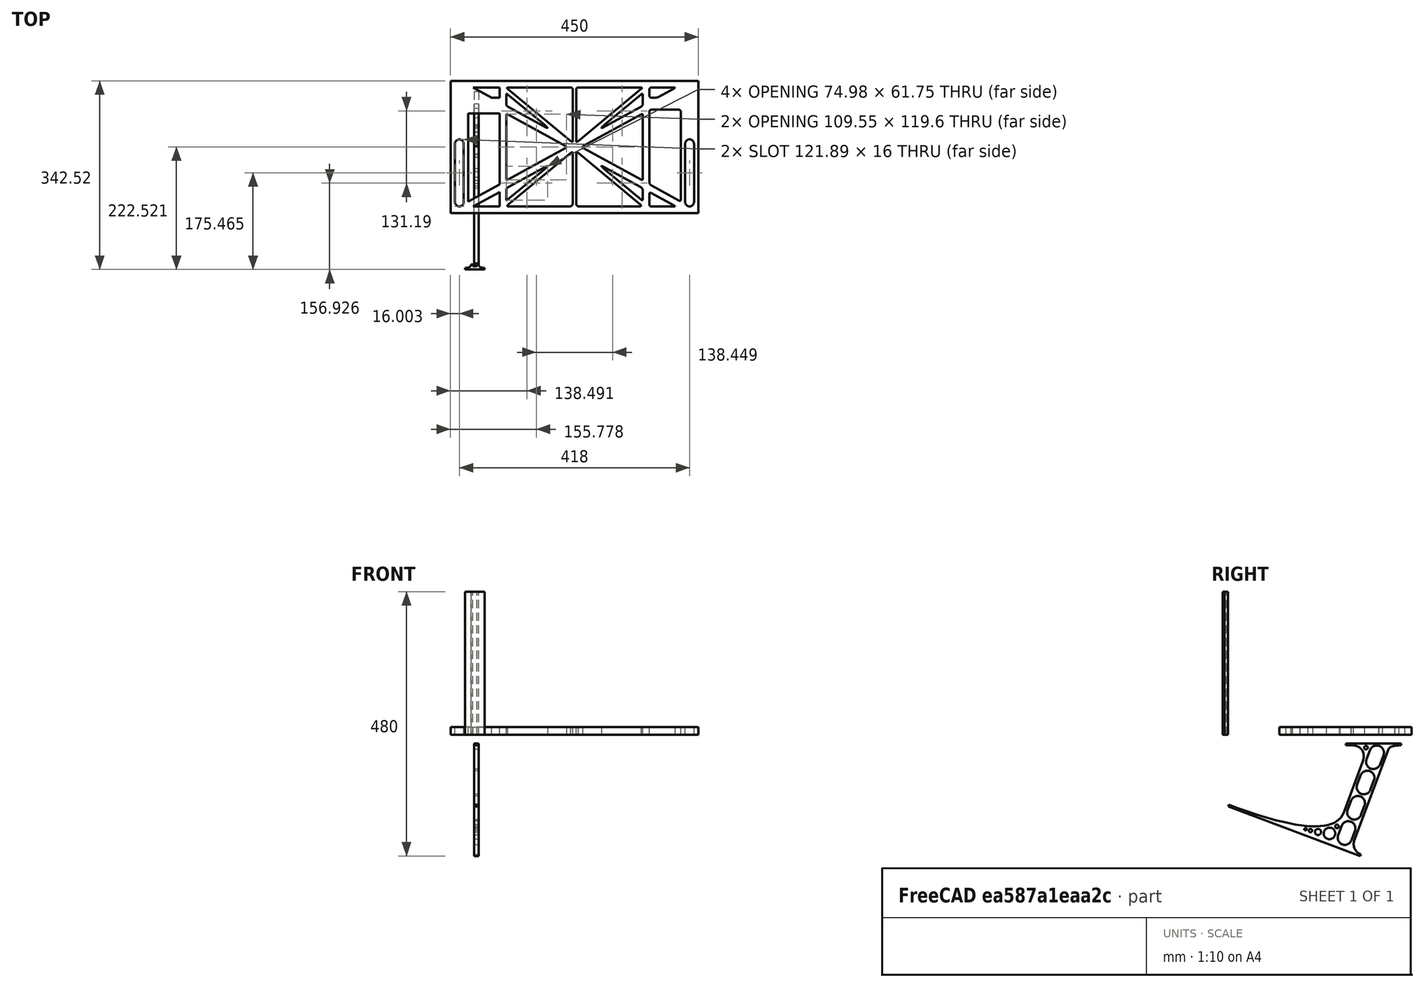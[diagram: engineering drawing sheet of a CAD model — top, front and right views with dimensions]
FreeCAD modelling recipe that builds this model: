
FCSTD DOCUMENT  (FreeCAD 0.19R0.19.2)
Label: laptopStand1155FCStd
License: All rights reserved
LicenseURL: http://en.wikipedia.org/wiki/All_rights_reserved
objects: Sketcher::SketchObject×3, Part::Extrusion×3
note: 6 computed .brp shape members not serialized (recipe doc carries the construction recipe); baked Part::Feature solids carry a one-line shape summary decoded from their .brp

FEATURE [Sketcher::SketchObject] Sketch
  FullyConstrained = true
  sketch-geometry (318):
    g0: LineSegment StartX=-10.9272 StartY=-82.7794 StartZ=0 EndX=46.0728 EndY=-51.4823 EndZ=0
    g1: LineSegment StartX=-10.9272 StartY=77.3346 StartZ=0 EndX=-10.9272 EndY=-82.7794 EndZ=0
    g2: LineSegment StartX=-1.92719 StartY=-91.7794 StartZ=0 EndX=46.0728 EndY=-91.7794 EndZ=0
    g3: LineSegment StartX=46.0728 StartY=-65.424 StartZ=0 EndX=-1.92719 EndY=-91.7794 EndZ=0
    g4: LineSegment StartX=46.0728 StartY=-65.424 StartZ=0 EndX=46.0728 EndY=-91.7794 EndZ=0
    g5: LineSegment StartX=46.0728 StartY=77.3346 StartZ=0 EndX=46.0728 EndY=-51.4823 EndZ=0
    g6: LineSegment StartX=-42.9272 StartY=136.221 StartZ=0 EndX=-42.9272 EndY=-103.779 EndZ=0
    g7: LineSegment StartX=407.073 StartY=136.221 StartZ=0 EndX=407.073 EndY=-103.779 EndZ=0
    g8: ArcOfCircle CenterX=-26.9272 CenterY=22.1087 CenterZ=0 NormalX=0 NormalY=0 NormalZ=1 AngleXU=0 Radius=8 StartAngle=1e-16 EndAngle=3.14159
    g9: ArcOfCircle CenterX=-26.9272 CenterY=-83.7794 CenterZ=0 NormalX=0 NormalY=0 NormalZ=1 AngleXU=0 Radius=8 StartAngle=3.14159 EndAngle=6.28319
    g10: LineSegment StartX=-34.9272 StartY=22.1087 StartZ=0 EndX=-34.9272 EndY=-83.7794 EndZ=0
    g11: LineSegment StartX=-18.9272 StartY=22.1087 StartZ=0 EndX=-18.9272 EndY=-83.7794 EndZ=0
    g12: ArcOfCircle CenterX=391.073 CenterY=22.1087 CenterZ=0 NormalX=0 NormalY=0 NormalZ=1 AngleXU=0 Radius=8 StartAngle=-4.4e-15 EndAngle=3.14159
    g13: LineSegment StartX=399.073 StartY=22.1087 StartZ=0 EndX=399.073 EndY=-83.7794 EndZ=0
    g14: LineSegment StartX=383.073 StartY=22.1087 StartZ=0 EndX=383.073 EndY=-83.7794 EndZ=0
    g15: ArcOfCircle CenterX=391.073 CenterY=-83.7794 CenterZ=0 NormalX=0 NormalY=0 NormalZ=1 AngleXU=0 Radius=8 StartAngle=3.14159 EndAngle=6.28319
    g16: Circle CenterX=175.022 CenterY=27.0628 CenterZ=0 NormalX=0 NormalY=0 NormalZ=1 AngleXU=0 Radius=1
    g17: Circle CenterX=179.022 CenterY=24.8665 CenterZ=0 NormalX=0 NormalY=0 NormalZ=1 AngleXU=0 Radius=1
    g18: Circle CenterX=179.022 CenterY=27.0628 CenterZ=0 NormalX=0 NormalY=0 NormalZ=1 AngleXU=0 Radius=1
    g19: BSplineCurve PolesCount=3 KnotsCount=2 Degree=2 IsPeriodic=0
    g20: GeomPoint X=175.022 Y=27.0628 Z=0
    g21: GeomPoint X=179.022 Y=27.0628 Z=0
    g22: Circle CenterX=189.124 CenterY=27.0628 CenterZ=0 NormalX=0 NormalY=0 NormalZ=1 AngleXU=0 Radius=1
    g23: Circle CenterX=185.124 CenterY=24.8665 CenterZ=0 NormalX=0 NormalY=0 NormalZ=1 AngleXU=0 Radius=1
    g24: Circle CenterX=185.124 CenterY=27.0628 CenterZ=0 NormalX=0 NormalY=0 NormalZ=1 AngleXU=0 Radius=1
    g25: BSplineCurve PolesCount=3 KnotsCount=2 Degree=2 IsPeriodic=0
    g26: GeomPoint X=189.124 Y=27.0628 Z=0
    g27: GeomPoint X=185.124 Y=27.0628 Z=0
    g28: Circle CenterX=175.022 CenterY=5.37834 CenterZ=0 NormalX=0 NormalY=0 NormalZ=1 AngleXU=0 Radius=1
    g29: Circle CenterX=179.022 CenterY=7.57463 CenterZ=0 NormalX=0 NormalY=0 NormalZ=1 AngleXU=0 Radius=1
    g30: Circle CenterX=179.022 CenterY=5.34704 CenterZ=0 NormalX=0 NormalY=0 NormalZ=1 AngleXU=0 Radius=1
    g31: BSplineCurve PolesCount=3 KnotsCount=2 Degree=2 IsPeriodic=0
    g32: GeomPoint X=175.022 Y=5.37834 Z=0
    g33: GeomPoint X=179.022 Y=5.34704 Z=0
    g34: Circle CenterX=189.124 CenterY=5.37834 CenterZ=0 NormalX=0 NormalY=0 NormalZ=1 AngleXU=0 Radius=1
    g35: Circle CenterX=185.124 CenterY=7.57463 CenterZ=0 NormalX=0 NormalY=0 NormalZ=1 AngleXU=0 Radius=1
    g36: Circle CenterX=185.124 CenterY=5.34704 CenterZ=0 NormalX=0 NormalY=0 NormalZ=1 AngleXU=0 Radius=1
    g37: BSplineCurve PolesCount=3 KnotsCount=2 Degree=2 IsPeriodic=0
    g38: GeomPoint X=189.124 Y=5.37834 Z=0
    g39: GeomPoint X=185.124 Y=5.34704 Z=0
    g40: Circle CenterX=165.871 CenterY=18.1458 CenterZ=0 NormalX=0 NormalY=0 NormalZ=1 AngleXU=0 Radius=1
    g41: Circle CenterX=169.377 CenterY=16.2206 CenterZ=0 NormalX=0 NormalY=0 NormalZ=1 AngleXU=0 Radius=1
    g42: Circle CenterX=165.871 CenterY=14.2954 CenterZ=0 NormalX=0 NormalY=0 NormalZ=1 AngleXU=0 Radius=1
    g43: BSplineCurve PolesCount=3 KnotsCount=2 Degree=2 IsPeriodic=0
    g44: GeomPoint X=165.871 Y=18.1458 Z=0
    g45: GeomPoint X=165.871 Y=14.2954 Z=0
    g46: Circle CenterX=198.275 CenterY=18.1458 CenterZ=0 NormalX=0 NormalY=0 NormalZ=1 AngleXU=0 Radius=1
    g47: Circle CenterX=194.768 CenterY=16.2206 CenterZ=0 NormalX=0 NormalY=0 NormalZ=1 AngleXU=0 Radius=1
    g48: Circle CenterX=198.275 CenterY=14.2954 CenterZ=0 NormalX=0 NormalY=0 NormalZ=1 AngleXU=0 Radius=1
    g49: BSplineCurve PolesCount=3 KnotsCount=2 Degree=2 IsPeriodic=0
    g50: GeomPoint X=198.275 Y=18.1458 Z=0
    g51: GeomPoint X=198.275 Y=14.2954 Z=0
    g52: LineSegment StartX=407.073 StartY=-103.779 StartZ=0 EndX=-42.9272 EndY=-103.779 EndZ=0
    g53: LineSegment StartX=407.073 StartY=136.221 StartZ=0 EndX=-42.9272 EndY=136.221 EndZ=0
    g54: LineSegment StartX=46.0728 StartY=77.3346 StartZ=0 EndX=-10.9272 EndY=77.3346 EndZ=0
    g55: LineSegment StartX=46.0728 StartY=105.865 StartZ=0 EndX=31.5028 EndY=105.865 EndZ=0
    g56: LineSegment StartX=46.0728 StartY=124.221 StartZ=0 EndX=46.0728 EndY=105.865 EndZ=0
    g57: LineSegment StartX=-1.92719 StartY=124.221 StartZ=0 EndX=31.5028 EndY=105.865 EndZ=0
    g58: LineSegment StartX=46.0728 StartY=124.221 StartZ=0 EndX=-1.92719 EndY=124.221 EndZ=0
    g59: Circle CenterX=125.607 CenterY=54.1951 CenterZ=0 NormalX=0 NormalY=0 NormalZ=1 AngleXU=0 Radius=1
    g60: Circle CenterX=139.632 CenterY=46.4944 CenterZ=0 NormalX=0 NormalY=0 NormalZ=1 AngleXU=0 Radius=1
    g61: Circle CenterX=127.326 CenterY=56.7187 CenterZ=0 NormalX=0 NormalY=0 NormalZ=1 AngleXU=0 Radius=1
    g62: BSplineCurve PolesCount=3 KnotsCount=2 Degree=2 IsPeriodic=0
    g63: GeomPoint X=125.607 Y=54.1951 Z=0
    g64: GeomPoint X=127.326 Y=56.7187 Z=0
    g65: Circle CenterX=236.821 CenterY=56.7187 CenterZ=0 NormalX=0 NormalY=0 NormalZ=1 AngleXU=0 Radius=1
    g66: Circle CenterX=224.513 CenterY=46.4944 CenterZ=0 NormalX=0 NormalY=0 NormalZ=1 AngleXU=0 Radius=1
    g67: Circle CenterX=238.538 CenterY=54.1951 CenterZ=0 NormalX=0 NormalY=0 NormalZ=1 AngleXU=0 Radius=1
    g68: BSplineCurve PolesCount=3 KnotsCount=2 Degree=2 IsPeriodic=0
    g69: GeomPoint X=236.821 Y=56.7187 Z=0
    g70: GeomPoint X=238.538 Y=54.1951 Z=0
    g71: Circle CenterX=238.538 CenterY=-21.7539 CenterZ=0 NormalX=0 NormalY=0 NormalZ=1 AngleXU=0 Radius=1
    g72: Circle CenterX=224.513 CenterY=-14.0532 CenterZ=0 NormalX=0 NormalY=0 NormalZ=1 AngleXU=0 Radius=1
    g73: Circle CenterX=236.821 CenterY=-24.2775 CenterZ=0 NormalX=0 NormalY=0 NormalZ=1 AngleXU=0 Radius=1
    g74: BSplineCurve PolesCount=3 KnotsCount=2 Degree=2 IsPeriodic=0
    g75: GeomPoint X=238.538 Y=-21.7539 Z=0
    g76: GeomPoint X=236.821 Y=-24.2775 Z=0
    g77: Circle CenterX=125.607 CenterY=-21.7539 CenterZ=0 NormalX=0 NormalY=0 NormalZ=1 AngleXU=0 Radius=1
    g78: Circle CenterX=139.632 CenterY=-14.0532 CenterZ=0 NormalX=0 NormalY=0 NormalZ=1 AngleXU=0 Radius=1
    g79: Circle CenterX=127.325 CenterY=-24.2775 CenterZ=0 NormalX=0 NormalY=0 NormalZ=1 AngleXU=0 Radius=1
    g80: BSplineCurve PolesCount=3 KnotsCount=2 Degree=2 IsPeriodic=0
    g81: GeomPoint X=125.607 Y=-21.7539 Z=0
    g82: GeomPoint X=127.325 Y=-24.2775 Z=0
    g83: Circle CenterX=302.996 CenterY=111.695 CenterZ=0 NormalX=0 NormalY=0 NormalZ=1 AngleXU=0 Radius=1
    g84: Circle CenterX=306.073 CenterY=114.251 CenterZ=0 NormalX=0 NormalY=0 NormalZ=1 AngleXU=0 Radius=1
    g85: Circle CenterX=306.073 CenterY=110.251 CenterZ=0 NormalX=0 NormalY=0 NormalZ=1 AngleXU=0 Radius=1
    g86: BSplineCurve PolesCount=3 KnotsCount=2 Degree=2 IsPeriodic=0
    g87: GeomPoint X=302.996 Y=111.695 Z=0
    g88: GeomPoint X=306.073 Y=110.251 Z=0
    g89: Circle CenterX=306.073 CenterY=95.2763 CenterZ=0 NormalX=0 NormalY=0 NormalZ=1 AngleXU=0 Radius=1
    g90: Circle CenterX=306.073 CenterY=91.2763 CenterZ=0 NormalX=0 NormalY=0 NormalZ=1 AngleXU=0 Radius=1
    g91: Circle CenterX=302.567 CenterY=89.3511 CenterZ=0 NormalX=0 NormalY=0 NormalZ=1 AngleXU=0 Radius=1
    g92: BSplineCurve PolesCount=3 KnotsCount=2 Degree=2 IsPeriodic=0
    g93: GeomPoint X=306.073 Y=95.2763 Z=0
    g94: GeomPoint X=302.567 Y=89.3511 Z=0
    g95: LineSegment StartX=306.073 StartY=110.251 StartZ=0 EndX=306.073 EndY=95.2763 EndZ=0
    g96: LineSegment StartX=302.996 StartY=111.695 StartZ=0 EndX=236.821 EndY=56.7187 EndZ=0
    g97: LineSegment StartX=238.538 StartY=54.1951 StartZ=0 EndX=302.567 EndY=89.3511 EndZ=0
    g98: Circle CenterX=61.1496 CenterY=111.695 CenterZ=0 NormalX=0 NormalY=0 NormalZ=1 AngleXU=0 Radius=1
    g99: Circle CenterX=58.0728 CenterY=114.251 CenterZ=0 NormalX=0 NormalY=0 NormalZ=1 AngleXU=0 Radius=1
    g100: Circle CenterX=58.0728 CenterY=110.251 CenterZ=0 NormalX=0 NormalY=0 NormalZ=1 AngleXU=0 Radius=1
    g101: BSplineCurve PolesCount=3 KnotsCount=2 Degree=2 IsPeriodic=0
    g102: GeomPoint X=61.1496 Y=111.695 Z=0
    g103: GeomPoint X=58.0728 Y=110.251 Z=0
    g104: Circle CenterX=61.5791 CenterY=89.3511 CenterZ=0 NormalX=0 NormalY=0 NormalZ=1 AngleXU=0 Radius=1
    g105: Circle CenterX=58.0728 CenterY=91.2763 CenterZ=0 NormalX=0 NormalY=0 NormalZ=1 AngleXU=0 Radius=1
    g106: Circle CenterX=58.0728 CenterY=95.2763 CenterZ=0 NormalX=0 NormalY=0 NormalZ=1 AngleXU=0 Radius=1
    g107: BSplineCurve PolesCount=3 KnotsCount=2 Degree=2 IsPeriodic=0
    g108: GeomPoint X=61.5791 Y=89.3511 Z=0
    g109: GeomPoint X=58.0728 Y=95.2763 Z=0
    g110: LineSegment StartX=58.0728 StartY=110.251 StartZ=0 EndX=58.0728 EndY=95.2763 EndZ=0
    g111: LineSegment StartX=61.1496 StartY=111.695 StartZ=0 EndX=127.326 EndY=56.7187 EndZ=0
    g112: LineSegment StartX=125.607 StartY=54.1951 StartZ=0 EndX=61.5791 EndY=89.3511 EndZ=0
    g113: Circle CenterX=61.5791 CenterY=-56.9099 CenterZ=0 NormalX=0 NormalY=0 NormalZ=1 AngleXU=0 Radius=1
    g114: Circle CenterX=58.0728 CenterY=-58.8351 CenterZ=0 NormalX=0 NormalY=0 NormalZ=1 AngleXU=0 Radius=1
    g115: Circle CenterX=58.0728 CenterY=-62.8351 CenterZ=0 NormalX=0 NormalY=0 NormalZ=1 AngleXU=0 Radius=1
    g116: BSplineCurve PolesCount=3 KnotsCount=2 Degree=2 IsPeriodic=0
    g117: GeomPoint X=61.5791 Y=-56.9099 Z=0
    g118: GeomPoint X=58.0728 Y=-62.8351 Z=0
    g119: Circle CenterX=58.0728 CenterY=-77.8102 CenterZ=0 NormalX=0 NormalY=0 NormalZ=1 AngleXU=0 Radius=1
    g120: Circle CenterX=58.0728 CenterY=-81.8102 CenterZ=0 NormalX=0 NormalY=0 NormalZ=1 AngleXU=0 Radius=1
    g121: Circle CenterX=61.1496 CenterY=-79.2541 CenterZ=0 NormalX=0 NormalY=0 NormalZ=1 AngleXU=0 Radius=1
    g122: BSplineCurve PolesCount=3 KnotsCount=2 Degree=2 IsPeriodic=0
    g123: GeomPoint X=58.0728 Y=-77.8102 Z=0
    g124: GeomPoint X=61.1496 Y=-79.2541 Z=0
    g125: LineSegment StartX=58.0728 StartY=-62.8351 StartZ=0 EndX=58.0728 EndY=-77.8102 EndZ=0
    g126: LineSegment StartX=61.1496 StartY=-79.2541 StartZ=0 EndX=127.325 EndY=-24.2775 EndZ=0
    g127: LineSegment StartX=125.607 StartY=-21.7539 StartZ=0 EndX=61.5791 EndY=-56.9099 EndZ=0
    g128: Circle CenterX=302.567 CenterY=-56.9099 CenterZ=0 NormalX=0 NormalY=0 NormalZ=1 AngleXU=0 Radius=1
    g129: Circle CenterX=306.073 CenterY=-58.8351 CenterZ=0 NormalX=0 NormalY=0 NormalZ=1 AngleXU=0 Radius=1
    g130: Circle CenterX=306.073 CenterY=-62.8351 CenterZ=0 NormalX=0 NormalY=0 NormalZ=1 AngleXU=0 Radius=1
    g131: BSplineCurve PolesCount=3 KnotsCount=2 Degree=2 IsPeriodic=0
    g132: GeomPoint X=302.567 Y=-56.9099 Z=0
    g133: GeomPoint X=306.073 Y=-62.8351 Z=0
    g134: Circle CenterX=302.996 CenterY=-79.2541 CenterZ=0 NormalX=0 NormalY=0 NormalZ=1 AngleXU=0 Radius=1
    g135: Circle CenterX=306.073 CenterY=-81.8102 CenterZ=0 NormalX=0 NormalY=0 NormalZ=1 AngleXU=0 Radius=1
    g136: Circle CenterX=306.073 CenterY=-77.8102 CenterZ=0 NormalX=0 NormalY=0 NormalZ=1 AngleXU=0 Radius=1
    g137: BSplineCurve PolesCount=3 KnotsCount=2 Degree=2 IsPeriodic=0
    g138: GeomPoint X=302.996 Y=-79.2541 Z=0
    g139: GeomPoint X=306.073 Y=-77.8102 Z=0
    g140: LineSegment StartX=306.073 StartY=-62.8351 StartZ=0 EndX=306.073 EndY=-77.8102 EndZ=0
    g141: LineSegment StartX=302.996 StartY=-79.2541 StartZ=0 EndX=236.821 EndY=-24.2775 EndZ=0
    g142: LineSegment StartX=238.538 StartY=-21.7539 StartZ=0 EndX=302.567 EndY=-56.9099 EndZ=0
    g143: Circle CenterX=61.6457 CenterY=-88.8112 CenterZ=0 NormalX=0 NormalY=0 NormalZ=1 AngleXU=0 Radius=1
    g144: Circle CenterX=58.0728 CenterY=-91.7794 CenterZ=0 NormalX=0 NormalY=0 NormalZ=1 AngleXU=0 Radius=1
    g145: Circle CenterX=63.9135 CenterY=-91.7794 CenterZ=0 NormalX=0 NormalY=0 NormalZ=1 AngleXU=0 Radius=1
    g146: BSplineCurve PolesCount=3 KnotsCount=2 Degree=2 IsPeriodic=0
    g147: GeomPoint X=61.6457 Y=-88.8112 Z=0
    g148: GeomPoint X=63.9135 Y=-91.7794 Z=0
    g149: Circle CenterX=179.022 CenterY=-85.8163 CenterZ=0 NormalX=0 NormalY=0 NormalZ=1 AngleXU=0 Radius=1
    g150: Circle CenterX=179.022 CenterY=-91.7794 CenterZ=0 NormalX=0 NormalY=0 NormalZ=1 AngleXU=0 Radius=1
    g151: Circle CenterX=171.895 CenterY=-91.7794 CenterZ=0 NormalX=0 NormalY=0 NormalZ=1 AngleXU=0 Radius=1
    g152: BSplineCurve PolesCount=3 KnotsCount=2 Degree=2 IsPeriodic=0
    g153: GeomPoint X=179.022 Y=-85.8163 Z=0
    g154: GeomPoint X=171.895 Y=-91.7794 Z=0
    g155: Circle CenterX=185.124 CenterY=-86.2028 CenterZ=0 NormalX=0 NormalY=0 NormalZ=1 AngleXU=0 Radius=1
    g156: Circle CenterX=185.124 CenterY=-91.7794 CenterZ=0 NormalX=0 NormalY=0 NormalZ=1 AngleXU=0 Radius=1
    g157: Circle CenterX=191.747 CenterY=-91.7794 CenterZ=0 NormalX=0 NormalY=0 NormalZ=1 AngleXU=0 Radius=1
    g158: BSplineCurve PolesCount=3 KnotsCount=2 Degree=2 IsPeriodic=0
    g159: GeomPoint X=185.124 Y=-86.2028 Z=0
    g160: GeomPoint X=191.747 Y=-91.7794 Z=0
    g161: Circle CenterX=299.888 CenterY=-86.6413 CenterZ=0 NormalX=0 NormalY=0 NormalZ=1 AngleXU=0 Radius=1
    g162: Circle CenterX=306.073 CenterY=-91.7794 CenterZ=0 NormalX=0 NormalY=0 NormalZ=1 AngleXU=0 Radius=1
    g163: Circle CenterX=298.776 CenterY=-91.7794 CenterZ=0 NormalX=0 NormalY=0 NormalZ=1 AngleXU=0 Radius=1
    g164: BSplineCurve PolesCount=3 KnotsCount=2 Degree=2 IsPeriodic=0
    g165: GeomPoint X=299.888 Y=-86.6413 Z=0
    g166: GeomPoint X=298.776 Y=-91.7794 Z=0
    g167: LineSegment StartX=189.124 StartY=5.37834 StartZ=0 EndX=299.888 EndY=-86.6413 EndZ=0
    g168: LineSegment StartX=298.776 StartY=-91.7794 StartZ=0 EndX=191.747 EndY=-91.7794 EndZ=0
    g169: LineSegment StartX=185.124 StartY=-86.2028 StartZ=0 EndX=185.124 EndY=5.34704 EndZ=0
    g170: LineSegment StartX=179.022 StartY=5.34704 StartZ=0 EndX=179.022 EndY=-85.8163 EndZ=0
    g171: LineSegment StartX=171.895 StartY=-91.7794 StartZ=0 EndX=63.9135 EndY=-91.7794 EndZ=0
    g172: LineSegment StartX=61.6457 StartY=-88.8112 StartZ=0 EndX=175.022 EndY=5.37834 EndZ=0
    g173: Circle CenterX=302.073 CenterY=124.221 CenterZ=0 NormalX=0 NormalY=0 NormalZ=1 AngleXU=0 Radius=1
    g174: Circle CenterX=306.073 CenterY=124.221 CenterZ=0 NormalX=0 NormalY=0 NormalZ=1 AngleXU=0 Radius=1
    g175: Circle CenterX=302.996 CenterY=121.665 CenterZ=0 NormalX=0 NormalY=0 NormalZ=1 AngleXU=0 Radius=1
    g176: BSplineCurve PolesCount=3 KnotsCount=2 Degree=2 IsPeriodic=0
    g177: GeomPoint X=302.073 Y=124.221 Z=0
    g178: GeomPoint X=302.996 Y=121.665 Z=0
    g179: Circle CenterX=189.124 CenterY=124.221 CenterZ=0 NormalX=0 NormalY=0 NormalZ=1 AngleXU=0 Radius=1
    g180: Circle CenterX=185.124 CenterY=124.221 CenterZ=0 NormalX=0 NormalY=0 NormalZ=1 AngleXU=0 Radius=1
    g181: Circle CenterX=185.124 CenterY=120.221 CenterZ=0 NormalX=0 NormalY=0 NormalZ=1 AngleXU=0 Radius=1
    g182: BSplineCurve PolesCount=3 KnotsCount=2 Degree=2 IsPeriodic=0
    g183: GeomPoint X=189.124 Y=124.221 Z=0
    g184: GeomPoint X=185.124 Y=120.221 Z=0
    g185: Circle CenterX=175.022 CenterY=124.221 CenterZ=0 NormalX=0 NormalY=0 NormalZ=1 AngleXU=0 Radius=1
    g186: Circle CenterX=179.022 CenterY=124.221 CenterZ=0 NormalX=0 NormalY=0 NormalZ=1 AngleXU=0 Radius=1
    g187: Circle CenterX=179.022 CenterY=120.221 CenterZ=0 NormalX=0 NormalY=0 NormalZ=1 AngleXU=0 Radius=1
    g188: BSplineCurve PolesCount=3 KnotsCount=2 Degree=2 IsPeriodic=0
    g189: GeomPoint X=175.022 Y=124.221 Z=0
    g190: GeomPoint X=179.022 Y=120.221 Z=0
    g191: Circle CenterX=62.0728 CenterY=124.221 CenterZ=0 NormalX=0 NormalY=0 NormalZ=1 AngleXU=0 Radius=1
    g192: Circle CenterX=58.0728 CenterY=124.221 CenterZ=0 NormalX=0 NormalY=0 NormalZ=1 AngleXU=0 Radius=1
    g193: Circle CenterX=61.1496 CenterY=121.665 CenterZ=0 NormalX=0 NormalY=0 NormalZ=1 AngleXU=0 Radius=1
    g194: BSplineCurve PolesCount=3 KnotsCount=2 Degree=2 IsPeriodic=0
    g195: GeomPoint X=62.0728 Y=124.221 Z=0
    g196: GeomPoint X=61.1496 Y=121.665 Z=0
    g197: LineSegment StartX=62.0728 StartY=124.221 StartZ=0 EndX=175.022 EndY=124.221 EndZ=0
    g198: LineSegment StartX=179.022 StartY=120.221 StartZ=0 EndX=179.022 EndY=27.0628 EndZ=0
    g199: LineSegment StartX=185.124 StartY=27.0628 StartZ=0 EndX=185.124 EndY=120.221 EndZ=0
    g200: LineSegment StartX=189.124 StartY=124.221 StartZ=0 EndX=302.073 EndY=124.221 EndZ=0
    g201: LineSegment StartX=302.996 StartY=121.665 StartZ=0 EndX=189.124 EndY=27.0628 EndZ=0
    g202: LineSegment StartX=175.022 StartY=27.0628 StartZ=0 EndX=61.1496 EndY=121.665 EndZ=0
    g203: Circle CenterX=61.5791 CenterY=75.4095 CenterZ=0 NormalX=0 NormalY=0 NormalZ=1 AngleXU=0 Radius=1
    g204: Circle CenterX=58.0728 CenterY=77.3346 CenterZ=0 NormalX=0 NormalY=0 NormalZ=1 AngleXU=0 Radius=1
    g205: Circle CenterX=58.0728 CenterY=73.3346 CenterZ=0 NormalX=0 NormalY=0 NormalZ=1 AngleXU=0 Radius=1
    g206: BSplineCurve PolesCount=3 KnotsCount=2 Degree=2 IsPeriodic=0
    g207: GeomPoint X=61.5791 Y=75.4095 Z=0
    g208: GeomPoint X=58.0728 Y=73.3346 Z=0
    g209: Circle CenterX=58.0728 CenterY=-40.8935 CenterZ=0 NormalX=0 NormalY=0 NormalZ=1 AngleXU=0 Radius=1
    g210: Circle CenterX=58.0728 CenterY=-44.8935 CenterZ=0 NormalX=0 NormalY=0 NormalZ=1 AngleXU=0 Radius=1
    g211: Circle CenterX=61.5791 CenterY=-42.9683 CenterZ=0 NormalX=0 NormalY=0 NormalZ=1 AngleXU=0 Radius=1
    g212: BSplineCurve PolesCount=3 KnotsCount=2 Degree=2 IsPeriodic=0
    g213: GeomPoint X=58.0728 Y=-40.8935 Z=0
    g214: GeomPoint X=61.5791 Y=-42.9683 Z=0
    g215: LineSegment StartX=61.5791 StartY=-42.9683 StartZ=0 EndX=165.871 EndY=14.2954 EndZ=0
    g216: LineSegment StartX=165.871 StartY=18.1458 StartZ=0 EndX=61.5791 EndY=75.4095 EndZ=0
    g217: LineSegment StartX=58.0728 StartY=73.3346 StartZ=0 EndX=58.0728 EndY=-40.8935 EndZ=0
    g218: Circle CenterX=302.567 CenterY=-42.9683 CenterZ=0 NormalX=0 NormalY=0 NormalZ=1 AngleXU=0 Radius=1
    g219: Circle CenterX=306.073 CenterY=-44.8935 CenterZ=0 NormalX=0 NormalY=0 NormalZ=1 AngleXU=0 Radius=1
    g220: Circle CenterX=306.073 CenterY=-40.8935 CenterZ=0 NormalX=0 NormalY=0 NormalZ=1 AngleXU=0 Radius=1
    g221: BSplineCurve PolesCount=3 KnotsCount=2 Degree=2 IsPeriodic=0
    g222: GeomPoint X=302.567 Y=-42.9683 Z=0
    g223: GeomPoint X=306.073 Y=-40.8935 Z=0
    g224: Circle CenterX=306.073 CenterY=73.3346 CenterZ=0 NormalX=0 NormalY=0 NormalZ=1 AngleXU=0 Radius=1
    g225: Circle CenterX=306.073 CenterY=77.3346 CenterZ=0 NormalX=0 NormalY=0 NormalZ=1 AngleXU=0 Radius=1
    g226: Circle CenterX=302.567 CenterY=75.4095 CenterZ=0 NormalX=0 NormalY=0 NormalZ=1 AngleXU=0 Radius=1
    g227: BSplineCurve PolesCount=3 KnotsCount=2 Degree=2 IsPeriodic=0
    g228: GeomPoint X=306.073 Y=73.3346 Z=0
    g229: GeomPoint X=302.567 Y=75.4095 Z=0
    g230: LineSegment StartX=302.567 StartY=-42.9683 StartZ=0 EndX=198.275 EndY=14.2954 EndZ=0
    g231: LineSegment StartX=198.275 StartY=18.1458 StartZ=0 EndX=302.567 EndY=75.4095 EndZ=0
    g232: LineSegment StartX=306.073 StartY=73.3346 StartZ=0 EndX=306.073 EndY=-40.8935 EndZ=0
    g233: LineSegment StartX=322.073 StartY=105.865 StartZ=0 EndX=328.643 EndY=105.865 EndZ=0
    g234: LineSegment StartX=318.073 StartY=120.221 StartZ=0 EndX=318.073 EndY=109.865 EndZ=0
    g235: LineSegment StartX=336.157 StartY=107.779 StartZ=0 EndX=362.567 EndY=122.294 EndZ=0
    g236: Circle CenterX=362.073 CenterY=124.221 CenterZ=0 NormalX=0 NormalY=0 NormalZ=1 AngleXU=0 Radius=1
    g237: Circle CenterX=366.073 CenterY=124.221 CenterZ=0 NormalX=0 NormalY=0 NormalZ=1 AngleXU=0 Radius=1
    g238: Circle CenterX=362.567 CenterY=122.294 CenterZ=0 NormalX=0 NormalY=0 NormalZ=1 AngleXU=0 Radius=1
    g239: BSplineCurve PolesCount=3 KnotsCount=2 Degree=2 IsPeriodic=0
    g240: GeomPoint X=362.073 Y=124.221 Z=0
    g241: GeomPoint X=362.567 Y=122.294 Z=0
    g242: Circle CenterX=322.073 CenterY=124.221 CenterZ=0 NormalX=0 NormalY=0 NormalZ=1 AngleXU=0 Radius=1
    g243: Circle CenterX=318.073 CenterY=124.221 CenterZ=0 NormalX=0 NormalY=0 NormalZ=1 AngleXU=0 Radius=1
    g244: Circle CenterX=318.073 CenterY=120.221 CenterZ=0 NormalX=0 NormalY=0 NormalZ=1 AngleXU=0 Radius=1
    g245: BSplineCurve PolesCount=3 KnotsCount=2 Degree=2 IsPeriodic=0
    g246: GeomPoint X=322.073 Y=124.221 Z=0
    g247: GeomPoint X=318.073 Y=120.221 Z=0
    g248: Circle CenterX=322.073 CenterY=105.865 CenterZ=0 NormalX=0 NormalY=0 NormalZ=1 AngleXU=0 Radius=1
    g249: Circle CenterX=318.073 CenterY=105.865 CenterZ=0 NormalX=0 NormalY=0 NormalZ=1 AngleXU=0 Radius=1
    g250: Circle CenterX=318.073 CenterY=109.865 CenterZ=0 NormalX=0 NormalY=0 NormalZ=1 AngleXU=0 Radius=1
    g251: BSplineCurve PolesCount=3 KnotsCount=2 Degree=2 IsPeriodic=0
    g252: GeomPoint X=322.073 Y=105.865 Z=0
    g253: GeomPoint X=318.073 Y=109.865 Z=0
    g254: Circle CenterX=336.157 CenterY=107.779 CenterZ=0 NormalX=0 NormalY=0 NormalZ=1 AngleXU=0 Radius=1
    g255: Circle CenterX=332.651 CenterY=105.853 CenterZ=0 NormalX=0 NormalY=0 NormalZ=1 AngleXU=0 Radius=1
    g256: Circle CenterX=328.643 CenterY=105.865 CenterZ=0 NormalX=0 NormalY=0 NormalZ=1 AngleXU=0 Radius=1
    g257: BSplineCurve PolesCount=3 KnotsCount=2 Degree=2 IsPeriodic=0
    g258: GeomPoint X=336.157 Y=107.779 Z=0
    g259: GeomPoint X=328.643 Y=105.865 Z=0
    g260: LineSegment StartX=322.073 StartY=124.221 StartZ=0 EndX=362.073 EndY=124.221 EndZ=0
    g261: Circle CenterX=371.567 CenterY=-80.8644 CenterZ=0 NormalX=0 NormalY=0 NormalZ=1 AngleXU=0 Radius=1
    g262: Circle CenterX=375.073 CenterY=-82.7896 CenterZ=0 NormalX=0 NormalY=0 NormalZ=1 AngleXU=0 Radius=1
    g263: Circle CenterX=375.073 CenterY=-78.7896 CenterZ=0 NormalX=0 NormalY=0 NormalZ=1 AngleXU=0 Radius=1
    g264: BSplineCurve PolesCount=3 KnotsCount=2 Degree=2 IsPeriodic=0
    g265: GeomPoint X=371.567 Y=-80.8644 Z=0
    g266: GeomPoint X=375.073 Y=-78.7896 Z=0
    g267: Circle CenterX=321.579 CenterY=-53.4075 CenterZ=0 NormalX=0 NormalY=0 NormalZ=1 AngleXU=0 Radius=1
    g268: Circle CenterX=318.073 CenterY=-51.4823 CenterZ=0 NormalX=0 NormalY=0 NormalZ=1 AngleXU=0 Radius=1
    g269: Circle CenterX=318.073 CenterY=-47.4823 CenterZ=0 NormalX=0 NormalY=0 NormalZ=1 AngleXU=0 Radius=1
    g270: BSplineCurve PolesCount=3 KnotsCount=2 Degree=2 IsPeriodic=0
    g271: GeomPoint X=321.579 Y=-53.4075 Z=0
    g272: GeomPoint X=318.073 Y=-47.4823 Z=0
    g273: Circle CenterX=318.073 CenterY=79.9235 CenterZ=0 NormalX=0 NormalY=0 NormalZ=1 AngleXU=0 Radius=1
    g274: Circle CenterX=318.073 CenterY=83.9235 CenterZ=0 NormalX=0 NormalY=0 NormalZ=1 AngleXU=0 Radius=1
    g275: Circle CenterX=322.073 CenterY=83.9235 CenterZ=0 NormalX=0 NormalY=0 NormalZ=1 AngleXU=0 Radius=1
    g276: BSplineCurve PolesCount=3 KnotsCount=2 Degree=2 IsPeriodic=0
    g277: GeomPoint X=318.073 Y=79.9235 Z=0
    g278: GeomPoint X=322.073 Y=83.9235 Z=0
    g279: Circle CenterX=375.073 CenterY=79.9235 CenterZ=0 NormalX=0 NormalY=0 NormalZ=1 AngleXU=0 Radius=1
    g280: Circle CenterX=375.073 CenterY=83.9235 CenterZ=0 NormalX=0 NormalY=0 NormalZ=1 AngleXU=0 Radius=1
    g281: Circle CenterX=371.073 CenterY=83.9235 CenterZ=0 NormalX=0 NormalY=0 NormalZ=1 AngleXU=0 Radius=1
    g282: BSplineCurve PolesCount=3 KnotsCount=2 Degree=2 IsPeriodic=0
    g283: GeomPoint X=375.073 Y=79.9235 Z=0
    g284: GeomPoint X=371.073 Y=83.9235 Z=0
    g285: LineSegment StartX=322.073 StartY=83.9235 StartZ=0 EndX=371.073 EndY=83.9235 EndZ=0
    g286: LineSegment StartX=375.073 StartY=79.9235 StartZ=0 EndX=375.073 EndY=-78.7896 EndZ=0
    g287: LineSegment StartX=371.567 StartY=-80.8644 StartZ=0 EndX=321.579 EndY=-53.4075 EndZ=0
    g288: LineSegment StartX=318.073 StartY=-47.4823 StartZ=0 EndX=318.073 EndY=79.9235 EndZ=0
    g289: Circle CenterX=321.579 CenterY=-67.3492 CenterZ=0 NormalX=0 NormalY=0 NormalZ=1 AngleXU=0 Radius=1
    g290: Circle CenterX=318.073 CenterY=-65.424 CenterZ=0 NormalX=0 NormalY=0 NormalZ=1 AngleXU=0 Radius=1
    g291: Circle CenterX=318.073 CenterY=-69.424 CenterZ=0 NormalX=0 NormalY=0 NormalZ=1 AngleXU=0 Radius=1
    g292: BSplineCurve PolesCount=3 KnotsCount=2 Degree=2 IsPeriodic=0
    g293: GeomPoint X=321.579 Y=-67.3492 Z=0
    g294: GeomPoint X=318.073 Y=-69.424 Z=0
    g295: Circle CenterX=362.567 CenterY=-89.8542 CenterZ=0 NormalX=0 NormalY=0 NormalZ=1 AngleXU=0 Radius=1
    g296: Circle CenterX=366.073 CenterY=-91.7794 CenterZ=0 NormalX=0 NormalY=0 NormalZ=1 AngleXU=0 Radius=1
    g297: Circle CenterX=362.073 CenterY=-91.7794 CenterZ=0 NormalX=0 NormalY=0 NormalZ=1 AngleXU=0 Radius=1
    g298: BSplineCurve PolesCount=3 KnotsCount=2 Degree=2 IsPeriodic=0
    g299: GeomPoint X=362.567 Y=-89.8542 Z=0
    g300: GeomPoint X=362.073 Y=-91.7794 Z=0
    g301: Circle CenterX=322.073 CenterY=-91.7794 CenterZ=0 NormalX=0 NormalY=0 NormalZ=1 AngleXU=0 Radius=1
    g302: Circle CenterX=318.073 CenterY=-91.7794 CenterZ=0 NormalX=0 NormalY=0 NormalZ=1 AngleXU=0 Radius=1
    g303: Circle CenterX=318.073 CenterY=-87.7794 CenterZ=0 NormalX=0 NormalY=0 NormalZ=1 AngleXU=0 Radius=1
    g304: BSplineCurve PolesCount=3 KnotsCount=2 Degree=2 IsPeriodic=0
    g305: GeomPoint X=322.073 Y=-91.7794 Z=0
    g306: GeomPoint X=318.073 Y=-87.7794 Z=0
    g307: LineSegment StartX=362.567 StartY=-89.8542 StartZ=0 EndX=321.579 EndY=-67.3492 EndZ=0
    g308: LineSegment StartX=318.073 StartY=-69.424 StartZ=0 EndX=318.073 EndY=-87.7794 EndZ=0
    g309: LineSegment StartX=322.073 StartY=-91.7794 StartZ=0 EndX=362.073 EndY=-91.7794 EndZ=0
    g310: LineSegment StartX=-1.92719 StartY=124.221 StartZ=0 EndX=2.07281 EndY=124.221 EndZ=0
    g311: LineSegment StartX=-1.92719 StartY=124.221 StartZ=0 EndX=1.57905 EndY=122.295 EndZ=0
    g312: LineSegment StartX=31.5028 StartY=105.865 StartZ=0 EndX=27.9965 EndY=107.79 EndZ=0
    g313: LineSegment StartX=31.5028 StartY=105.865 StartZ=0 EndX=35.5028 EndY=105.865 EndZ=0
    g314: LineSegment StartX=46.0728 StartY=105.865 StartZ=0 EndX=42.0728 EndY=105.865 EndZ=0
    g315: LineSegment StartX=46.0728 StartY=105.865 StartZ=0 EndX=46.0728 EndY=109.865 EndZ=0
    g316: LineSegment StartX=46.0728 StartY=124.221 StartZ=0 EndX=46.0728 EndY=120.221 EndZ=0
    g317: LineSegment StartX=46.0728 StartY=124.221 StartZ=0 EndX=42.0728 EndY=124.221 EndZ=0
  constraints (543):
    c: Horizontal(g2)
    c: Coincident(g4,g3)
    c: Coincident(g0,g5)
    c: Block(g4)
    c: Block(g3)
    c: Block(g0)
    c: Block(g1)
    c: Block(g2)
    c: Vertical(g6)
    c: Vertical(g7)
    c: Block(g7)
    c: Block(g6)
    c: Tangent(g8,g11) = 1.5708
    c: Tangent(g8,g10) = -1.5708
    c: Tangent(g10,g9) = -1.5708
    c: Tangent(g11,g9) = 1.5708
    c: Vertical(g10)
    c: Equal(g8,g9)
    c: Block(g11)
    c: Block(g10)
    c: Tangent(g12,g13) = 1.5708
    c: Tangent(g13,g15) = 1.5708
    c: Equal(g12,g15)
    c: Coincident(g14,g12)
    c: Coincident(g14,g15)
    c: Block(g13)
    c: Block(g14)
    c: Weight(g16) = 1
    c: Equal(g16,g17)
    c: Equal(g16,g18)
    c: InternalAlignment(g16,g19)
    c: InternalAlignment(g17,g19)
    c: InternalAlignment(g18,g19)
    c: InternalAlignment(g20,g19)
    c: InternalAlignment(g21,g19)
    c: Weight(g22) = 1
    c: Equal(g22,g23)
    c: Equal(g22,g24)
    c: InternalAlignment(g22,g25)
    c: InternalAlignment(g23,g25)
    c: InternalAlignment(g24,g25)
    c: InternalAlignment(g26,g25)
    c: InternalAlignment(g27,g25)
    c: Block(g25)
    c: Block(g19)
    c: Weight(g28) = 1
    c: Equal(g28,g29)
    c: Equal(g28,g30)
    c: InternalAlignment(g28,g31)
    c: InternalAlignment(g29,g31)
    c: InternalAlignment(g30,g31)
    c: InternalAlignment(g32,g31)
    c: InternalAlignment(g33,g31)
    c: Weight(g34) = 1
    c: Equal(g34,g35)
    c: Equal(g34,g36)
    c: InternalAlignment(g34,g37)
    c: InternalAlignment(g35,g37)
    c: InternalAlignment(g36,g37)
    c: InternalAlignment(g38,g37)
    c: InternalAlignment(g39,g37)
    c: Block(g37)
    c: Block(g31)
    c: Weight(g40) = 1
    c: Equal(g40,g41)
    c: Equal(g40,g42)
    c: InternalAlignment(g40,g43)
    c: InternalAlignment(g41,g43)
    c: InternalAlignment(g42,g43)
    c: InternalAlignment(g44,g43)
    c: InternalAlignment(g45,g43)
    c: Weight(g46) = 1
    c: Equal(g46,g47)
    c: Equal(g46,g48)
    c: InternalAlignment(g46,g49)
    c: InternalAlignment(g47,g49)
    c: InternalAlignment(g48,g49)
    c: InternalAlignment(g50,g49)
    c: InternalAlignment(g51,g49)
    c: Block(g43)
    c: Block(g49)
    c: Coincident(g52,g7)
    c: Coincident(g52,g6)
    c: Horizontal(g52)
    c: Distance(g52) = 450
    c: Coincident(g53,g7)
    c: Coincident(g53,g6)
    c: Horizontal(g53)
    c: Horizontal(g54)
    c: Coincident(g5,g54)
    c: Horizontal(g55)
    c: Vertical(g56)
    c: Block(g56)
    c: Block(g55)
    c: Block(g54)
    c: Distance(g56) = 18.3554
    c: Coincident(g58,g56)
    c: Coincident(g58,g57)
    c: Horizontal(g58)
    c: Block(g58)
    c: Block(g57)
    c: Coincident(g55,g57)
    c: Coincident(g1,g54)
    c: Weight(g59) = 1
    c: Equal(g59,g60)
    c: Equal(g59,g61)
    c: InternalAlignment(g59,g62)
    c: InternalAlignment(g60,g62)
    c: InternalAlignment(g61,g62)
    c: InternalAlignment(g63,g62)
    c: InternalAlignment(g64,g62)
    c: Block(g62)
    c: Weight(g65) = 1
    c: Equal(g65,g66)
    c: Equal(g65,g67)
    c: InternalAlignment(g65,g68)
    c: InternalAlignment(g66,g68)
    c: InternalAlignment(g67,g68)
    c: InternalAlignment(g69,g68)
    c: InternalAlignment(g70,g68)
    c: Block(g68)
    c: Weight(g71) = 1
    c: Equal(g71,g72)
    c: Equal(g71,g73)
    c: InternalAlignment(g71,g74)
    c: InternalAlignment(g72,g74)
    c: InternalAlignment(g73,g74)
    c: InternalAlignment(g75,g74)
    c: InternalAlignment(g76,g74)
    c: Block(g74)
    c: Weight(g77) = 1
    c: Equal(g77,g78)
    c: Equal(g77,g79)
    c: InternalAlignment(g77,g80)
    c: InternalAlignment(g78,g80)
    c: InternalAlignment(g79,g80)
    c: InternalAlignment(g81,g80)
    c: InternalAlignment(g82,g80)
    c: Block(g80)
    c: Weight(g83) = 1
    c: Equal(g83,g84)
    c: Equal(g83,g85)
    c: InternalAlignment(g83,g86)
    c: InternalAlignment(g84,g86)
    c: InternalAlignment(g85,g86)
    c: InternalAlignment(g87,g86)
    c: InternalAlignment(g88,g86)
    c: Weight(g89) = 1
    c: Equal(g89,g90)
    c: Equal(g89,g91)
    c: InternalAlignment(g89,g92)
    c: InternalAlignment(g90,g92)
    c: InternalAlignment(g91,g92)
    c: InternalAlignment(g93,g92)
    c: InternalAlignment(g94,g92)
    c: Block(g86)
    c: Block(g92)
    c: Coincident(g95,g86)
    c: Coincident(g95,g92)
    c: Vertical(g95)
    c: Coincident(g96,g86)
    c: Coincident(g96,g68)
    c: Coincident(g97,g68)
    c: Coincident(g97,g92)
    c: Weight(g98) = 1
    c: Equal(g98,g99)
    c: Equal(g98,g100)
    c: InternalAlignment(g98,g101)
    c: InternalAlignment(g99,g101)
    c: InternalAlignment(g100,g101)
    c: InternalAlignment(g102,g101)
    c: InternalAlignment(g103,g101)
    c: Weight(g104) = 1
    c: Equal(g104,g105)
    c: Equal(g104,g106)
    c: InternalAlignment(g104,g107)
    c: InternalAlignment(g105,g107)
    c: InternalAlignment(g106,g107)
    c: InternalAlignment(g108,g107)
    c: InternalAlignment(g109,g107)
    c: Block(g101)
    c: Block(g107)
    c: Coincident(g110,g101)
    c: Coincident(g110,g107)
    c: Vertical(g110)
    c: Coincident(g111,g101)
    c: Coincident(g111,g62)
    c: Coincident(g112,g62)
    c: Coincident(g112,g107)
    c: Weight(g113) = 1
    c: Equal(g113,g114)
    c: Equal(g113,g115)
    c: InternalAlignment(g113,g116)
    c: InternalAlignment(g114,g116)
    c: InternalAlignment(g115,g116)
    c: InternalAlignment(g117,g116)
    c: InternalAlignment(g118,g116)
    c: Weight(g119) = 1
    c: Equal(g119,g120)
    c: Equal(g119,g121)
    c: InternalAlignment(g119,g122)
    c: InternalAlignment(g120,g122)
    c: InternalAlignment(g121,g122)
    c: InternalAlignment(g123,g122)
    c: InternalAlignment(g124,g122)
    c: Block(g116)
    c: Block(g122)
    c: Coincident(g125,g116)
    c: Coincident(g125,g122)
    c: Vertical(g125)
    c: Coincident(g126,g122)
    c: Coincident(g126,g80)
    c: Coincident(g127,g80)
    c: Coincident(g127,g116)
    c: Weight(g128) = 1
    c: Equal(g128,g129)
    c: Equal(g128,g130)
    c: InternalAlignment(g128,g131)
    c: InternalAlignment(g129,g131)
    c: InternalAlignment(g130,g131)
    c: InternalAlignment(g132,g131)
    c: InternalAlignment(g133,g131)
    c: Weight(g134) = 1
    c: Equal(g134,g135)
    c: Equal(g134,g136)
    c: InternalAlignment(g134,g137)
    c: InternalAlignment(g135,g137)
    c: InternalAlignment(g136,g137)
    c: InternalAlignment(g138,g137)
    c: InternalAlignment(g139,g137)
    c: Block(g131)
    c: Block(g137)
    c: Coincident(g140,g131)
    c: Coincident(g140,g137)
    c: Vertical(g140)
    c: Coincident(g141,g137)
    c: Coincident(g141,g74)
    c: Coincident(g142,g74)
    c: Coincident(g142,g131)
    c: Weight(g143) = 1
    c: Equal(g143,g144)
    c: Equal(g143,g145)
    c: InternalAlignment(g143,g146)
    c: InternalAlignment(g144,g146)
    c: InternalAlignment(g145,g146)
    c: InternalAlignment(g147,g146)
    c: InternalAlignment(g148,g146)
    c: Weight(g149) = 1
    c: Equal(g149,g150)
    c: Equal(g149,g151)
    c: InternalAlignment(g149,g152)
    c: InternalAlignment(g150,g152)
    c: InternalAlignment(g151,g152)
    c: InternalAlignment(g153,g152)
    c: InternalAlignment(g154,g152)
    c: Weight(g155) = 1
    c: Equal(g155,g156)
    c: Equal(g155,g157)
    c: InternalAlignment(g155,g158)
    c: InternalAlignment(g156,g158)
    c: InternalAlignment(g157,g158)
    c: InternalAlignment(g159,g158)
    c: InternalAlignment(g160,g158)
    c: Weight(g161) = 1
    c: Equal(g161,g162)
    c: Equal(g161,g163)
    c: InternalAlignment(g161,g164)
    c: InternalAlignment(g162,g164)
    c: InternalAlignment(g163,g164)
    c: InternalAlignment(g165,g164)
    c: InternalAlignment(g166,g164)
    c: Block(g164)
    c: Block(g158)
    c: Block(g152)
    c: Block(g146)
    c: Coincident(g167,g37)
    c: Coincident(g167,g164)
    c: Coincident(g168,g164)
    c: Coincident(g168,g158)
    c: Horizontal(g168)
    c: Coincident(g169,g158)
    c: Coincident(g169,g37)
    c: Vertical(g169)
    c: Coincident(g170,g31)
    c: Coincident(g170,g152)
    c: Vertical(g170)
    c: Coincident(g171,g152)
    c: Coincident(g171,g146)
    c: Horizontal(g171)
    c: Coincident(g172,g146)
    c: Coincident(g172,g31)
    c: Weight(g173) = 1
    c: Equal(g173,g174)
    c: Equal(g173,g175)
    c: InternalAlignment(g173,g176)
    c: InternalAlignment(g174,g176)
    c: InternalAlignment(g175,g176)
    c: InternalAlignment(g177,g176)
    c: InternalAlignment(g178,g176)
    c: Weight(g179) = 1
    c: Equal(g179,g180)
    c: Equal(g179,g181)
    c: InternalAlignment(g179,g182)
    c: InternalAlignment(g180,g182)
    c: InternalAlignment(g181,g182)
    c: InternalAlignment(g183,g182)
    c: InternalAlignment(g184,g182)
    c: Weight(g185) = 1
    c: Equal(g185,g186)
    c: Equal(g185,g187)
    c: InternalAlignment(g185,g188)
    c: InternalAlignment(g186,g188)
    c: InternalAlignment(g187,g188)
    c: InternalAlignment(g189,g188)
    c: InternalAlignment(g190,g188)
    c: Weight(g191) = 1
    c: Equal(g191,g192)
    c: Equal(g191,g193)
    c: InternalAlignment(g191,g194)
    c: InternalAlignment(g192,g194)
    c: InternalAlignment(g193,g194)
    c: InternalAlignment(g195,g194)
    c: InternalAlignment(g196,g194)
    c: Block(g194)
    c: Block(g188)
    c: Block(g182)
    c: Block(g176)
    c: Coincident(g197,g194)
    c: Coincident(g197,g188)
    c: Horizontal(g197)
    c: Coincident(g198,g188)
    c: Coincident(g198,g19)
    c: Vertical(g198)
    c: Coincident(g199,g25)
    c: Coincident(g199,g182)
    c: Vertical(g199)
    c: Coincident(g200,g182)
    c: Coincident(g200,g176)
    c: Horizontal(g200)
    c: Coincident(g201,g176)
    c: Coincident(g201,g25)
    c: Coincident(g202,g19)
    c: Weight(g203) = 1
    c: Equal(g203,g204)
    c: Equal(g203,g205)
    c: InternalAlignment(g203,g206)
    c: InternalAlignment(g204,g206)
    c: InternalAlignment(g205,g206)
    c: InternalAlignment(g207,g206)
    c: InternalAlignment(g208,g206)
    c: Weight(g209) = 1
    c: Equal(g209,g210)
    c: Equal(g209,g211)
    c: InternalAlignment(g209,g212)
    c: InternalAlignment(g210,g212)
    c: InternalAlignment(g211,g212)
    c: InternalAlignment(g213,g212)
    c: InternalAlignment(g214,g212)
    c: Block(g212)
    c: Block(g206)
    c: Coincident(g215,g212)
    c: Coincident(g215,g43)
    c: Coincident(g216,g43)
    c: Coincident(g216,g206)
    c: Coincident(g217,g206)
    c: Coincident(g217,g212)
    c: Vertical(g217)
    c: Weight(g218) = 1
    c: Equal(g218,g219)
    c: Equal(g218,g220)
    c: InternalAlignment(g218,g221)
    c: InternalAlignment(g219,g221)
    c: InternalAlignment(g220,g221)
    c: InternalAlignment(g222,g221)
    c: InternalAlignment(g223,g221)
    c: Weight(g224) = 1
    c: Equal(g224,g225)
    c: Equal(g224,g226)
    c: InternalAlignment(g224,g227)
    c: InternalAlignment(g225,g227)
    c: InternalAlignment(g226,g227)
    c: InternalAlignment(g228,g227)
    c: InternalAlignment(g229,g227)
    c: Block(g227)
    c: Block(g221)
    c: Coincident(g230,g221)
    c: Coincident(g230,g49)
    c: Coincident(g231,g49)
    c: Coincident(g231,g227)
    c: Coincident(g232,g227)
    c: Coincident(g232,g221)
    c: Vertical(g232)
    c: Horizontal(g233)
    c: Block(g233)
    c: Vertical(g234)
    c: Block(g234)
    c: Block(g235)
    c: Weight(g236) = 1
    c: Equal(g236,g237)
    c: Equal(g236,g238)
    c: InternalAlignment(g236,g239)
    c: InternalAlignment(g237,g239)
    c: InternalAlignment(g238,g239)
    c: InternalAlignment(g240,g239)
    c: InternalAlignment(g241,g239)
    c: Weight(g242) = 1
    c: Equal(g242,g243)
    c: Equal(g242,g244)
    c: InternalAlignment(g242,g245)
    c: InternalAlignment(g243,g245)
    c: InternalAlignment(g244,g245)
    c: InternalAlignment(g246,g245)
    c: InternalAlignment(g247,g245)
    c: Weight(g248) = 1
    c: Equal(g248,g249)
    c: Equal(g248,g250)
    c: InternalAlignment(g248,g251)
    c: InternalAlignment(g249,g251)
    c: InternalAlignment(g250,g251)
    c: InternalAlignment(g252,g251)
    c: InternalAlignment(g253,g251)
    c: Weight(g254) = 1
    c: Equal(g254,g255)
    c: Equal(g254,g256)
    c: InternalAlignment(g254,g257)
    c: InternalAlignment(g255,g257)
    c: InternalAlignment(g256,g257)
    c: InternalAlignment(g258,g257)
    c: InternalAlignment(g259,g257)
    c: Block(g239)
    c: Block(g245)
    c: Block(g251)
    c: Block(g257)
    c: Coincident(g260,g245)
    c: Coincident(g260,g239)
    c: Horizontal(g260)
    c: Block(g202)
    c: Weight(g261) = 1
    c: Equal(g261,g262)
    c: Equal(g261,g263)
    c: InternalAlignment(g261,g264)
    c: InternalAlignment(g262,g264)
    c: InternalAlignment(g263,g264)
    c: InternalAlignment(g265,g264)
    c: InternalAlignment(g266,g264)
    c: Weight(g267) = 1
    c: Equal(g267,g268)
    c: Equal(g267,g269)
    c: InternalAlignment(g267,g270)
    c: InternalAlignment(g268,g270)
    c: InternalAlignment(g269,g270)
    c: InternalAlignment(g271,g270)
    c: InternalAlignment(g272,g270)
    c: Weight(g273) = 1
    c: Equal(g273,g274)
    c: Equal(g273,g275)
    c: InternalAlignment(g273,g276)
    c: InternalAlignment(g274,g276)
    c: InternalAlignment(g275,g276)
    c: InternalAlignment(g277,g276)
    c: InternalAlignment(g278,g276)
    c: Weight(g279) = 1
    c: Equal(g279,g280)
    c: Equal(g279,g281)
    c: InternalAlignment(g279,g282)
    c: InternalAlignment(g280,g282)
    c: InternalAlignment(g281,g282)
    c: InternalAlignment(g283,g282)
    c: InternalAlignment(g284,g282)
    c: Block(g264)
    c: Block(g270)
    c: Block(g276)
    c: Block(g282)
    c: Coincident(g285,g276)
    c: Coincident(g285,g282)
    c: Horizontal(g285)
    c: Coincident(g286,g282)
    c: Coincident(g286,g264)
    c: Vertical(g286)
    c: Coincident(g287,g264)
    c: Coincident(g287,g270)
    c: Coincident(g288,g270)
    c: Coincident(g288,g276)
    c: Vertical(g288)
    c: Weight(g289) = 1
    c: Equal(g289,g290)
    c: Equal(g289,g291)
    c: InternalAlignment(g289,g292)
    c: InternalAlignment(g290,g292)
    c: InternalAlignment(g291,g292)
    c: InternalAlignment(g293,g292)
    c: InternalAlignment(g294,g292)
    c: Weight(g295) = 1
    c: Equal(g295,g296)
    c: Equal(g295,g297)
    c: InternalAlignment(g295,g298)
    c: InternalAlignment(g296,g298)
    c: InternalAlignment(g297,g298)
    c: InternalAlignment(g299,g298)
    c: InternalAlignment(g300,g298)
    c: Weight(g301) = 1
    c: Equal(g301,g302)
    c: Equal(g301,g303)
    c: InternalAlignment(g301,g304)
    c: InternalAlignment(g302,g304)
    c: InternalAlignment(g303,g304)
    c: InternalAlignment(g305,g304)
    c: InternalAlignment(g306,g304)
    c: Block(g304)
    c: Block(g298)
    c: Block(g292)
    c: Coincident(g307,g298)
    c: Coincident(g307,g292)
    c: Coincident(g308,g292)
    c: Coincident(g308,g304)
    c: Vertical(g308)
    c: Coincident(g309,g304)
    c: Coincident(g309,g298)
    c: Horizontal(g309)
    c: Horizontal(g310)
    c: Horizontal(g313)
    c: Horizontal(g314)
    c: Vertical(g315)
    c: Vertical(g316)
    c: Horizontal(g317)
    c: Distance(g316) = 4
    c: Distance(g317) = 4
    c: Distance(g315) = 4
    c: Distance(g314) = 4
    c: Distance(g313) = 4
    c: Distance(g312) = 4
    c: Distance(g311) = 4
    c: Distance(g310) = 4
    c: Parallel(g57,g311)
    c: Parallel(g57,g312)
    c: Coincident(g312,g55)
    c: Coincident(g313,g55)
    c: Coincident(g314,g315)
    c: Coincident(g314,g55)
    c: Coincident(g316,g317)
    c: Coincident(g56,g316)
    c: Coincident(g310,g311)
    c: Coincident(g310,g57)
FEATURE [Sketcher::SketchObject] Sketch001
  FullyConstrained = true
  MapMode = 4
  Placement = pos=(0,0,0) rot=(0.57735,0.57735,0.57735;2.0944rad)
  Support = -> [Sketch]
  sketch-geometry (46):
    g0: BSplineCurve PolesCount=3 KnotsCount=2 Degree=2 IsPeriodic=0
    g1: ArcOfCircle CenterX=73.1223 CenterY=-32.291 CenterZ=0 NormalX=0 NormalY=0 NormalZ=1 AngleXU=0 Radius=13 StartAngle=5.92268 EndAngle=9.06428
    g2: ArcOfCircle CenterX=66.7816 CenterY=-49.1439 CenterZ=0 NormalX=0 NormalY=0 NormalZ=1 AngleXU=0 Radius=13 StartAngle=2.78068 EndAngle=5.92131
    g3: ArcOfCircle CenterX=55.9263 CenterY=-78.1807 CenterZ=0 NormalX=0 NormalY=0 NormalZ=1 AngleXU=0 Radius=13 StartAngle=5.92268 EndAngle=9.06428
    g4: ArcOfCircle CenterX=49.5884 CenterY=-95.0342 CenterZ=0 NormalX=0 NormalY=0 NormalZ=1 AngleXU=0 Radius=13 StartAngle=2.78068 EndAngle=5.92131
    g5: ArcOfCircle CenterX=38.7206 CenterY=-124.067 CenterZ=0 NormalX=0 NormalY=0 NormalZ=1 AngleXU=0 Radius=13 StartAngle=5.92268 EndAngle=9.06428
    g6: ArcOfCircle CenterX=32.3875 CenterY=-140.92 CenterZ=0 NormalX=0 NormalY=0 NormalZ=1 AngleXU=0 Radius=13 StartAngle=2.78068 EndAngle=5.92131
    g7: ArcOfCircle CenterX=21.4715 CenterY=-169.934 CenterZ=0 NormalX=0 NormalY=0 NormalZ=1 AngleXU=0 Radius=13 StartAngle=5.92268 EndAngle=9.06428
    g8: ArcOfCircle CenterX=15.1336 CenterY=-186.787 CenterZ=0 NormalX=0 NormalY=0 NormalZ=1 AngleXU=0 Radius=13 StartAngle=2.78068 EndAngle=5.92131
    g9-g12: Circle x4 (B-spline internal-alignment scaffolding for g13; pole/knot coordinates omitted)
    g13: BSplineCurve PolesCount=4 KnotsCount=2 Degree=3 IsPeriodic=0
    g14: GeomPoint X=28.8094 Y=-19.0875 Z=0
    g15: GeomPoint X=47.0443 Y=-50.4712 Z=0
    g16: Circle CenterX=53.5586 CenterY=-23.2695 CenterZ=0 NormalX=0 NormalY=0 NormalZ=1 AngleXU=0 Radius=3.24518
    g17: Circle CenterX=-195.441 CenterY=-127.082 CenterZ=0 NormalX=0 NormalY=0 NormalZ=1 AngleXU=0 Radius=1
    g18: Circle CenterX=-8.24091 CenterY=-197.481 CenterZ=0 NormalX=0 NormalY=0 NormalZ=1 AngleXU=0 Radius=1
    g19: Circle CenterX=12.8789 CenterY=-141.321 CenterZ=0 NormalX=0 NormalY=0 NormalZ=1 AngleXU=0 Radius=1
    g20: BSplineCurve PolesCount=3 KnotsCount=2 Degree=2 IsPeriodic=0
    g21: GeomPoint X=-195.441 Y=-127.082 Z=0
    g22: GeomPoint X=12.8789 Y=-141.321 Z=0
    g23: Circle CenterX=-12.8016 CenterY=-179.036 CenterZ=0 NormalX=0 NormalY=0 NormalZ=1 AngleXU=0 Radius=10.5072
    g24: Circle CenterX=0.933922 CenterY=-166.43 CenterZ=0 NormalX=0 NormalY=0 NormalZ=1 AngleXU=0 Radius=3.26661
    g25: Circle CenterX=-33.5518 CenterY=-176.44 CenterZ=0 NormalX=0 NormalY=0 NormalZ=1 AngleXU=0 Radius=5.64388
    g26: Circle CenterX=-47.2366 CenterY=-173.859 CenterZ=0 NormalX=0 NormalY=0 NormalZ=1 AngleXU=0 Radius=3.01653
    g27: Circle CenterX=-56.2595 CenterY=-171.456 CenterZ=0 NormalX=0 NormalY=0 NormalZ=1 AngleXU=0 Radius=2.12826
    g28: ArcOfCircle CenterX=51.2151 CenterY=-198.473 CenterZ=0 NormalX=0 NormalY=0 NormalZ=1 AngleXU=0 Radius=20 StartAngle=2.78189 EndAngle=4.35269
    g29: LineSegment StartX=32.4951 StartY=-191.433 StartZ=0 EndX=94.6578 EndY=-26.1352 EndZ=0
    g30: LineSegment StartX=43.1192 StartY=-220.001 StartZ=0 EndX=-196.497 EndY=-129.89 EndZ=0
    g31: LineSegment StartX=43.1192 StartY=-220.001 StartZ=0 EndX=44.1752 EndY=-217.193 EndZ=0
    g32: LineSegment StartX=117.223 StartY=-19.0875 StartZ=0 EndX=117.223 EndY=-16.0875 EndZ=0
    g33: LineSegment StartX=117.223 StartY=-16.0875 StartZ=0 EndX=17.2232 EndY=-16.0875 EndZ=0
    g34: LineSegment StartX=17.2232 StartY=-16.0875 StartZ=0 EndX=17.2232 EndY=-19.0875 EndZ=0
    g35: LineSegment StartX=28.8094 StartY=-19.0875 StartZ=0 EndX=17.2232 EndY=-19.0875 EndZ=0
    g36: LineSegment StartX=47.0443 StartY=-50.4712 StartZ=0 EndX=12.8789 EndY=-141.321 EndZ=0
    g37: LineSegment StartX=-195.441 StartY=-127.082 StartZ=0 EndX=-196.497 EndY=-129.89 EndZ=0
    g38: LineSegment StartX=85.2866 StartY=-36.8766 StartZ=0 EndX=78.9396 EndY=-53.7463 EndZ=0
    g39: LineSegment StartX=60.9579 StartY=-27.7053 StartZ=0 EndX=54.6191 EndY=-44.5532 EndZ=0
    g40: LineSegment StartX=68.0907 StartY=-82.7664 StartZ=0 EndX=61.7465 EndY=-99.6365 EndZ=0
    g41: LineSegment StartX=43.7619 StartY=-73.595 StartZ=0 EndX=37.426 EndY=-90.4435 EndZ=0
    g42: LineSegment StartX=50.885 StartY=-128.652 StartZ=0 EndX=44.5456 EndY=-145.522 EndZ=0
    g43: LineSegment StartX=26.5562 StartY=-119.481 StartZ=0 EndX=20.2251 EndY=-136.329 EndZ=0
    g44: LineSegment StartX=9.3071 StartY=-165.349 StartZ=0 EndX=2.97115 EndY=-182.197 EndZ=0
    g45: LineSegment StartX=33.6358 StartY=-174.52 StartZ=0 EndX=27.2917 EndY=-191.39 EndZ=0
  constraints (71):
    c: Block(g0)
    c: Block(g1)
    c: Block(g2)
    c: Block(g4)
    c: Block(g3)
    c: Block(g6)
    c: Block(g5)
    c: Block(g8)
    c: Block(g7)
    c: Weight(g9) = 1
    c: Equal(g9,g10)
    c: Equal(g9,g11)
    c: Equal(g9,g12)
    c: InternalAlignment(g9-g12 -> g13) x4
    c: InternalAlignment(g14,g13)
    c: InternalAlignment(g15,g13)
    c: Block(g16)
    c: Weight(g17) = 1
    c: Equal(g17,g18)
    c: Equal(g17,g19)
    c: InternalAlignment(g17,g20)
    c: InternalAlignment(g18,g20)
    c: InternalAlignment(g19,g20)
    c: InternalAlignment(g21,g20)
    c: InternalAlignment(g22,g20)
    c: Block(g20)
    c: Block(g23)
    c: Block(g24)
    c: Block(g25)
    c: Block(g26)
    c: Block(g27)
    c: Block(g28)
    c: Coincident(g29,g28)
    c: Coincident(g29,g0)
    c: Block(g13)
    c: Coincident(g31,g30)
    c: Coincident(g31,g28)
    c: Block(g31)
    c: Coincident(g32,g0)
    c: Vertical(g32)
    c: Coincident(g33,g32)
    c: Horizontal(g33)
    c: Coincident(g34,g33)
    c: Vertical(g34)
    c: Block(g33)
    c: Coincident(g35,g13)
    c: Coincident(g35,g34)
    c: Horizontal(g35)
    c: Coincident(g36,g13)
    c: Coincident(g36,g20)
    c: Coincident(g37,g20)
    c: Coincident(g37,g30)
    c: Block(g30)
    c: Coincident(g38,g1)
    c: Coincident(g38,g2)
    c: Coincident(g39,g1)
    c: Coincident(g39,g2)
    c: Coincident(g40,g3)
    c: Coincident(g40,g4)
    c: Coincident(g41,g3)
    c: Coincident(g41,g4)
    c: Coincident(g42,g5)
    c: Coincident(g42,g6)
    c: Coincident(g43,g5)
    c: Coincident(g43,g6)
    c: Coincident(g44,g7)
    c: Coincident(g44,g8)
    c: Coincident(g45,g7)
    c: Coincident(g45,g8)
    c: Distance(g30) = 256
    c: Distance(g33) = 100
FEATURE [Part::Extrusion] Extrude002
  Base = -> Sketch001
  Dir = (1,0,0)
  DirMode = 2
  FaceMakerClass = Part::FaceMakerBullseye
  LengthFwd = 8
  LengthRev = 0
  Solid = true
  Symmetric = false
FEATURE [Sketcher::SketchObject] Sketch002
  FullyConstrained = true
  sketch-geometry (20):
    g0: LineSegment StartX=-2.77179 StartY=-200.304 StartZ=0 EndX=5.22821 EndY=-200.304 EndZ=0
    g1: LineSegment StartX=5.22821 StartY=-200.304 StartZ=0 EndX=5.22821 EndY=-197.304 EndZ=0
    g2: LineSegment StartX=-2.77179 StartY=-200.304 StartZ=0 EndX=-2.77179 EndY=-197.304 EndZ=0
    g3: LineSegment StartX=5.22821 StartY=-197.304 StartZ=0 EndX=8.22821 EndY=-197.304 EndZ=0
    g4: LineSegment StartX=-2.77179 StartY=-197.304 StartZ=0 EndX=-5.77179 EndY=-197.304 EndZ=0
    g5: LineSegment StartX=19.2282 StartY=-203.304 StartZ=0 EndX=19.2282 EndY=-206.304 EndZ=0
    g6: LineSegment StartX=-16.7718 StartY=-203.304 StartZ=0 EndX=-16.7718 EndY=-206.304 EndZ=0
    g7: LineSegment StartX=-16.7718 StartY=-206.304 StartZ=0 EndX=19.2282 EndY=-206.304 EndZ=0
    g8: Circle CenterX=-16.7718 CenterY=-203.304 CenterZ=0 NormalX=0 NormalY=0 NormalZ=1 AngleXU=0 Radius=1
    g9: Circle CenterX=-5.77179 CenterY=-203.304 CenterZ=0 NormalX=0 NormalY=0 NormalZ=1 AngleXU=0 Radius=1
    g10: Circle CenterX=-5.77179 CenterY=-197.304 CenterZ=0 NormalX=0 NormalY=0 NormalZ=1 AngleXU=0 Radius=1
    g11: BSplineCurve PolesCount=3 KnotsCount=2 Degree=2 IsPeriodic=0
    g12: GeomPoint X=-16.7718 Y=-203.304 Z=0
    g13: GeomPoint X=-5.77179 Y=-197.304 Z=0
    g14: Circle CenterX=19.2282 CenterY=-203.304 CenterZ=0 NormalX=0 NormalY=0 NormalZ=1 AngleXU=0 Radius=1
    g15: Circle CenterX=8.22821 CenterY=-203.304 CenterZ=0 NormalX=0 NormalY=0 NormalZ=1 AngleXU=0 Radius=1
    g16: Circle CenterX=8.22821 CenterY=-197.304 CenterZ=0 NormalX=0 NormalY=0 NormalZ=1 AngleXU=0 Radius=1
    g17: BSplineCurve PolesCount=3 KnotsCount=2 Degree=2 IsPeriodic=0
    g18: GeomPoint X=19.2282 Y=-203.304 Z=0
    g19: GeomPoint X=8.22821 Y=-197.304 Z=0
  constraints (41):
    c: Horizontal(g0)
    c: Distance(g0) = 8
    c: Coincident(g1,g0)
    c: Vertical(g1)
    c: Distance(g1) = 3
    c: Coincident(g2,g0)
    c: Vertical(g2)
    c: Distance(g2) = 3
    c: Coincident(g3,g1)
    c: Horizontal(g3)
    c: Distance(g3) = 3
    c: Coincident(g4,g2)
    c: Horizontal(g4)
    c: Distance(g4) = 3
    c: Vertical(g5)
    c: Vertical(g6)
    c: Coincident(g7,g6)
    c: Coincident(g7,g5)
    c: Weight(g8) = 1
    c: Equal(g8,g9)
    c: Equal(g8,g10)
    c: Coincident(g11,g4)
    c: InternalAlignment(g8,g11)
    c: InternalAlignment(g9,g11)
    c: InternalAlignment(g10,g11)
    c: InternalAlignment(g12,g11)
    c: InternalAlignment(g13,g11)
    c: Coincident(g17,g5)
    c: Weight(g14) = 1
    c: Equal(g14,g15)
    c: Equal(g14,g16)
    c: Coincident(g17,g3)
    c: InternalAlignment(g14,g17)
    c: InternalAlignment(g15,g17)
    c: InternalAlignment(g16,g17)
    c: InternalAlignment(g18,g17)
    c: InternalAlignment(g19,g17)
    c: Block(g7)
    c: Block(g17)
    c: Block(g11)
    c: Block(g6)
FEATURE [Part::Extrusion] Extrude003
  Base = -> Sketch002
  Dir = (0,0,1)
  DirMode = 2
  FaceMakerClass = Part::FaceMakerBullseye
  LengthFwd = 260
  LengthRev = 0
  Solid = true
  Symmetric = false
FEATURE [Part::Extrusion] Extrude
  Base = -> Sketch
  Dir = (0,0,1)
  DirMode = 2
  FaceMakerClass = Part::FaceMakerBullseye
  LengthFwd = 14
  LengthRev = 0
  Solid = true
  Symmetric = false
